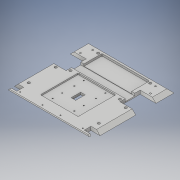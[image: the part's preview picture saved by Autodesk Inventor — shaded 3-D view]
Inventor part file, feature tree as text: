
AUTODESK INVENTOR PART (.ipt)
format: ipt  version: 2019 (Build 230136000, 136)  size: 469,504 bytes
history: native  units: in
note: dims shown in document units (in); Inventor stores cm internally (conversion verified against a paired STEP export)
features: sketch x17, extrude x16, move_body x10, direct_edit x5, hole x4, fillet x2
ambient origin geometry x8: Origin, YZ Plane, XZ Plane, XY Plane, X Axis, Y Axis, Z Axis, Center Point
bodies: Solid1 (feature_tree)
feature tree (54):
  extrude  "Extrusion1"  Depth=7.0866in
  extrude  "Extrusion2"  Depth=0.5906in
  extrude  "Extrusion3"  Depth=0.315in TaperAngle=0.0deg
  extrude  "Extrusion4"  Depth=0.315in
  extrude  "Extrusion7"  Depth=0.1969in TaperAngle=0.0deg
  fillet  "Fillet1"  Radius=2.441in
  extrude  "Extrusion8"  Depth=0.2165in TaperAngle=0.0deg
  direct_edit  "Direct Edit1"
  direct_edit  "Direct Edit2"
  fillet  "Fillet2"  Radius=0.1772in
  hole  "Hole1"  [1 undecoded]
  direct_edit  "Direct Edit3"
  hole  "Hole2"  [1 undecoded]
  hole  "Hole3"  [1 undecoded]
  extrude  "Extrusion9"  Depth=0.1181in
  extrude  "Extrusion10"  Depth=1.5748in
  extrude  "Extrusion11"  Depth=0.1181in TaperAngle=0.0deg
  extrude  "Extrusion12"  TaperAngle=0.0deg  [1 undecoded]
  extrude  "Extrusion13"  Depth=0.0787in
  extrude  "Extrusion14"  Depth=0.1969in
  extrude  "Extrusion15"  Depth=0.0984in TaperAngle=0.0deg
  extrude  "Extrusion16"  Depth=0.0984in TaperAngle=0.0deg
  extrude  "Extrusion17"  Depth=0.0984in TaperAngle=0.0deg
  hole  "Hole4"  [1 undecoded]
  extrude  "Extrusion18"  Depth=0.1969in
  direct_edit  "Direct Edit4"
  direct_edit  "Direct Edit5"
  sketch  "Sketch1"  dims[d0=7.0866in d1=7.0866in]
  sketch  "Sketch4"  dims[d2=0.1575in d3=0.5906in]
  sketch  "Sketch5"  dims[d4=0.5906in d5=0.315in d6=0.0in]
  sketch  "Sketch9"  dims[d12=0.315in d13=0.0in d14=7.087in]
  sketch  "Sketch11"  dims[d15=0.3583in d16=0.1969in d17=0.0in d19=2.441in]
  sketch  "Sketch15"  dims[d21=2.441in d23=0.2165in d24=0.0in d38=0.1772in d39=0.0in]
  sketch  "Sketch16"  dims[d40=1.1811in d41=3.3071in]
  sketch  "Sketch17"  dims[d42=1.9685in d43=0.1181in]
  sketch  "Sketch19"  dims[d45=0.1181in d46=0.0787in]
  sketch  "Sketch20"  dims[d47=0.8071in d48=0.1181in]
  sketch  "Sketch21"  dims[d49=1.5748in d50=3.1496in]
  sketch  "Sketch22"  dims[d51=3.1496in d52=0.1181in d53=0.0in]
  sketch  "Sketch23"  dims[d54=0.0in d55=0.0in d56=-0.1575in d57=0.0in d58=0.0in d59=-0.0787in]
  sketch  "Sketch24"  dims[d60=0.0in d61=0.0in d62=-0.0787in d63=0.0787in]
  sketch  "Sketch25"  dims[d64=0.1181in d65=0.1969in]
  sketch  "Sketch26"  dims[d66=1.9685in]
  sketch  "Sketch27"  dims[d67=0.097in d68=0.236in d69=0.248in d70=0.25in d71=90.0deg d72=0.346in d73=0.8108in d74=0.0in d75=0.0in d76=0.0984in d77=0.0in d78=0.0in d79=0.0984in d80=0.0in d81=0.0in d82=0.0984in d83=0.0in d84=0.0in d85=0.0984in d86=0.626in d87=0.2126in d88=1.8976in d89=0.097in d90=0.236in d91=0.248in d92=0.25in d93=90.0deg d94=0.346in d95=0.8108in d123=0.2126in d124=0.75in d125=0.409in d126=0.25in d127=90.0deg d128=1.0in d129=0.8108in d133=0.1181in d134=45.0deg d135=0.1181in d136=7.0866in d137=0.0in d138=0.1181in d139=0.528in d140=45.0deg d141=0.1181in d142=7.0866in d143=0.0in d148=7.0866in d149=0.0in d152=0.1575in d153=0.0in d154=0.584in d155=45.0deg d156=6.6929in d157=0.0in d158=30.0in d159=0.0in d160=30.0in d161=0.0in d162=0.0591in d163=0.0591in d164=7.874in d165=0.0in d166=0.0787in d167=0.0787in d168=40.0in d169=0.0in d170=0.0394in d171=0.1181in d172=0.1181in d173=0.0787in d174=0.1969in d175=0.1969in d176=0.1181in d177=0.2362in d178=0.1339in d179=0.75in d180=0.2717in d181=0.25in d182=0.563in d183=1.0in d184=0.8108in d185=0.748in d186=0.0787in d187=0.2756in d188=1.0in d189=0.0in d190=0.0in d191=0.0in d192=0.0394in d193=0.0in d194=0.0in d195=0.0394in d196=0.0in d197=0.0in d198=-0.375in d199=3.0709in d200=0.1969in d201=2.7559in d202=0.9646in]
  move_body  "Move1"
  move_body  "Move2"
  move_body  "Move3"
  move_body  "Move4"
  move_body  "Move5"
  move_body  "Move6"
  move_body  "Move7"
  move_body  "Move8"
  move_body  "Move9"
  move_body  "Move10"
note: 5 required parameter values undecoded (feature->parameter linkage not recoverable at this tier; creation-order binding heuristic only, values carry confidence <= 0.55)
